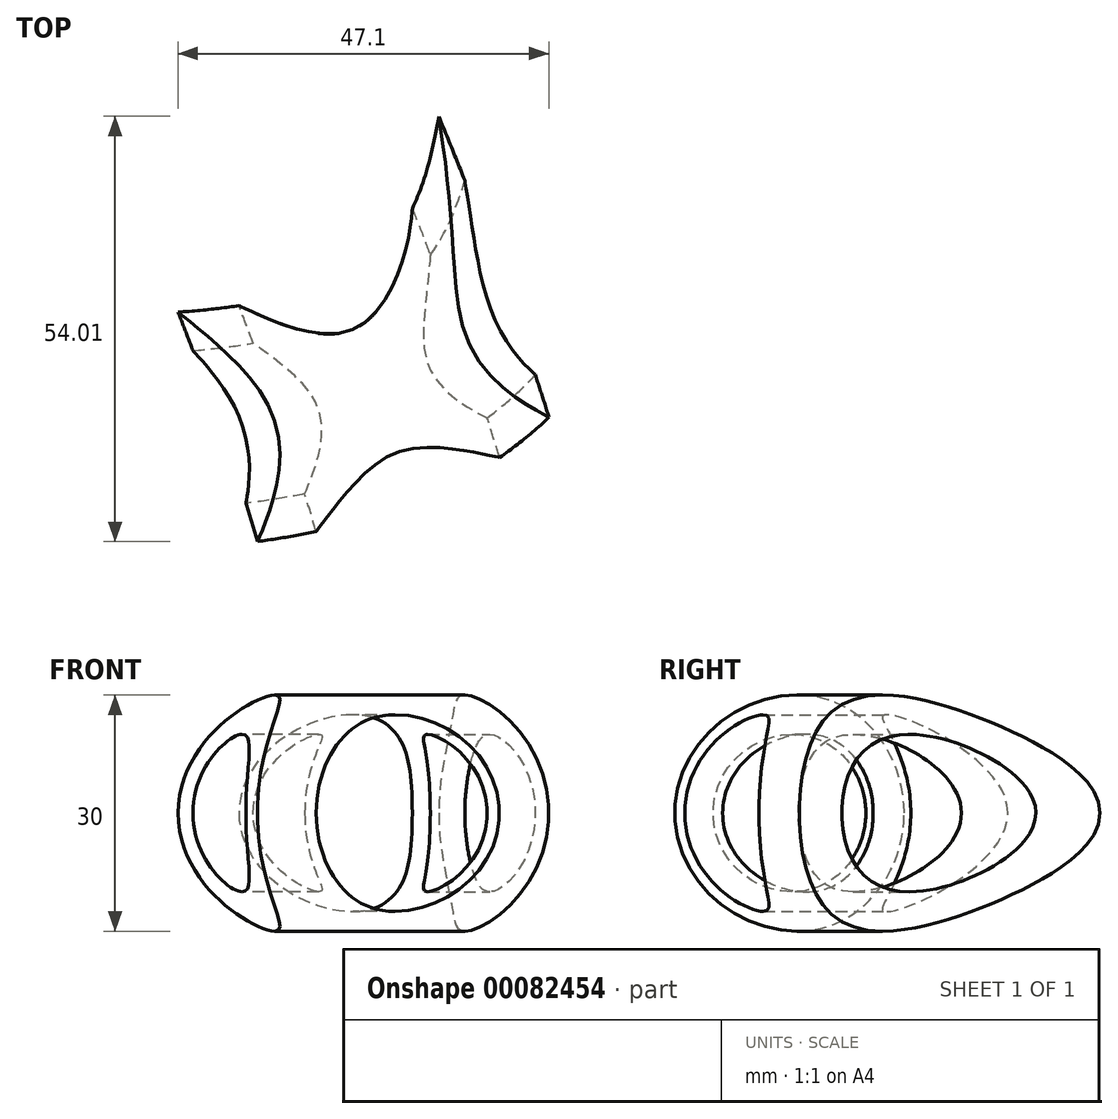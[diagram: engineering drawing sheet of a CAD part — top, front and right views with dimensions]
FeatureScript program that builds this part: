
annotation { "Feature Type Name" : "Feature", "Feature Type Description" : "" }
export const myFeature = defineFeature(function(context is Context, id is Id, definition is map)
    precondition{}
    {
        {
            var Q0;
            Q0=qCreatedBy(makeId("Top.planeOp"),FACE);
            var sketch = newSketch(context, id + "F0", { "sketchPlane" : qUnion([Q0])});
            skFitSpline(sketch, "E0", {"points": [v(-107.63, -69.48) * mm, v(-19.63, -52.63) * mm, v(-6, 64.44) * mm, v(57.52, 109.37) * mm], "startDerivative": vector(341.87, -25.58) * mm, "endDerivative": vector(266.96, 91.38) * mm});
            skFitSpline(sketch, "E1", {"points": [v(-6, 64.44) * mm, v(34.83, 52.44) * mm, v(65.1, 7.52) * mm], "startDerivative": vector(93.9, -11.62) * mm, "endDerivative": vector(49.2, -100.43) * mm});
            skFitSpline(sketch, "E2", {"points": [v(-24.9, -215.99) * mm, v(-26.9, -98.34) * mm, v(-107.76, 83.73) * mm], "startDerivative": vector(25.5, 259.6) * mm, "endDerivative": vector(-182.15, 336.49) * mm});
            skSolve(sketch);
        }
        {
            var Q0;
            Q0=sQuery(id+"F0.wireOp",VERTEX,"E0.start");
            var Q1;
            Q1=sQuery(id+"F0.wireOp",EDGE,"E0");
            cPlane(context, id + "F1", {"entities" : qUnion([Q0, Q1]), "cplaneType" : CPlaneType.CURVE_POINT, "offset" : 25 * mm, "width" : 150 * mm, "height" : 150 * mm});
        }
        {
            var Q0;
            Q0=qCreatedBy(id+"F1.planeOp",FACE);
            var sketch = newSketch(context, id + "F2", { "sketchPlane" : qUnion([Q0])});
            skCircle(sketch, "E3", {"center": v(-77.31, 0) * mm, "radius": 15 * mm});
            skCircle(sketch, "E4", {"center": v(-77.31, 0) * mm, "radius": 10 * mm});
            skSolve(sketch);
        }
        {
            var Q0;
            Q0=makeQuery(id+"F2.imprint","IMPRINT",FACE,{"disambiguationData":[TD([[makeQuery(id+"F2.imprint","IMPRINT",EDGE,{"derivedFrom":sQuery(id+"F2.wireOp",EDGE,"E3")}),1.0]])]});
            var Q1;
            Q1=sQuery(id+"F0.wireOp",EDGE,"E0");
            sweep(context, id + "F3", {"profiles" : qUnion([Q0]), "path" : qUnion([Q1])});
        }
        {
            var Q0;
            Q0=sQuery(id+"F0.wireOp",EDGE,"E1");
            var Q1;
            Q1=sQuery(id+"F0.wireOp",VERTEX,"E1.2.internal");
            cPlane(context, id + "F4", {"entities" : qUnion([Q0, Q1]), "cplaneType" : CPlaneType.CURVE_POINT, "offset" : 25 * mm, "width" : 150 * mm, "height" : 150 * mm});
        }
        {
            var Q0;
            Q0=qCreatedBy(id+"F4.planeOp",FACE);
            var sketch = newSketch(context, id + "F5", { "sketchPlane" : qUnion([Q0])});
            skCircle(sketch, "E5", {"center": v(61.77, 0) * mm, "radius": 7.5 * mm});
            skCircle(sketch, "E6", {"center": v(61.77, 0) * mm, "radius": 10 * mm});
            skSolve(sketch);
        }
        {
            var Q0;
            Q0=makeQuery(id+"F5.imprint","IMPRINT",FACE,{"disambiguationData":[TD([[makeQuery(id+"F5.imprint","IMPRINT",EDGE,{"derivedFrom":sQuery(id+"F5.wireOp",EDGE,"E5")}),-1.0]])]});
            var Q1;
            Q1=sQuery(id+"F0.wireOp",EDGE,"E1");
            sweep(context, id + "F6", {"operationType" : NewBodyOperationType.ADD, "profiles" : qUnion([Q0]), "path" : qUnion([Q1])});
        }
        {
            var Q0;
            Q0=makeQuery(id+"F2.imprint","IMPRINT",FACE,{"disambiguationData":[TD([[makeQuery(id+"F2.imprint","IMPRINT",EDGE,{"derivedFrom":sQuery(id+"F2.wireOp",EDGE,"E4")}),1.0]])]});
            var Q1;
            Q1=sQuery(id+"F0.wireOp",EDGE,"E0");
            sweep(context, id + "F7", {"operationType" : NewBodyOperationType.REMOVE, "profiles" : qUnion([Q0]), "path" : qUnion([Q1])});
        }
        {
            var Q0;
            Q0=makeQuery(id+"F5.imprint","IMPRINT",FACE,{"disambiguationData":[TD([[makeQuery(id+"F5.imprint","IMPRINT",EDGE,{"derivedFrom":sQuery(id+"F5.wireOp",EDGE,"E5")}),1.0]])]});
            var Q1;
            Q1=sQuery(id+"F0.wireOp",EDGE,"E1");
            sweep(context, id + "F8", {"operationType" : NewBodyOperationType.REMOVE, "profiles" : qUnion([Q0]), "path" : qUnion([Q1])});
        }
        {
            var Q0;
            Q0=sQuery(id+"F0.wireOp",VERTEX,"E2.0.internal");
            var Q1;
            Q1=sQuery(id+"F0.wireOp",EDGE,"E2");
            cPlane(context, id + "F9", {"entities" : qUnion([Q0, Q1]), "cplaneType" : CPlaneType.CURVE_POINT, "offset" : 25 * mm, "width" : 150 * mm, "height" : 150 * mm});
        }
        {
            var Q0;
            Q0=qCreatedBy(id+"F9.planeOp",FACE);
            var sketch = newSketch(context, id + "F10", { "sketchPlane" : qUnion([Q0])});
            skCircle(sketch, "E7", {"center": v(3.67, 0) * mm, "radius": 20 * mm});
            skCircle(sketch, "E8", {"center": v(3.67, 0) * mm, "radius": 12.5 * mm});
            skSolve(sketch);
        }
        {
            var Q0;
            Q0=makeQuery(id+"F10.imprint","IMPRINT",FACE,{"disambiguationData":[TD([[makeQuery(id+"F10.imprint","IMPRINT",EDGE,{"derivedFrom":sQuery(id+"F10.wireOp",EDGE,"E7")}),1.0]])]});
            var Q1;
            Q1=sQuery(id+"F0.wireOp",EDGE,"E2");
            sweep(context, id + "F11", {"operationType" : NewBodyOperationType.INTERSECT, "profiles" : qUnion([Q0]), "path" : qUnion([Q1])});
        }
    });
